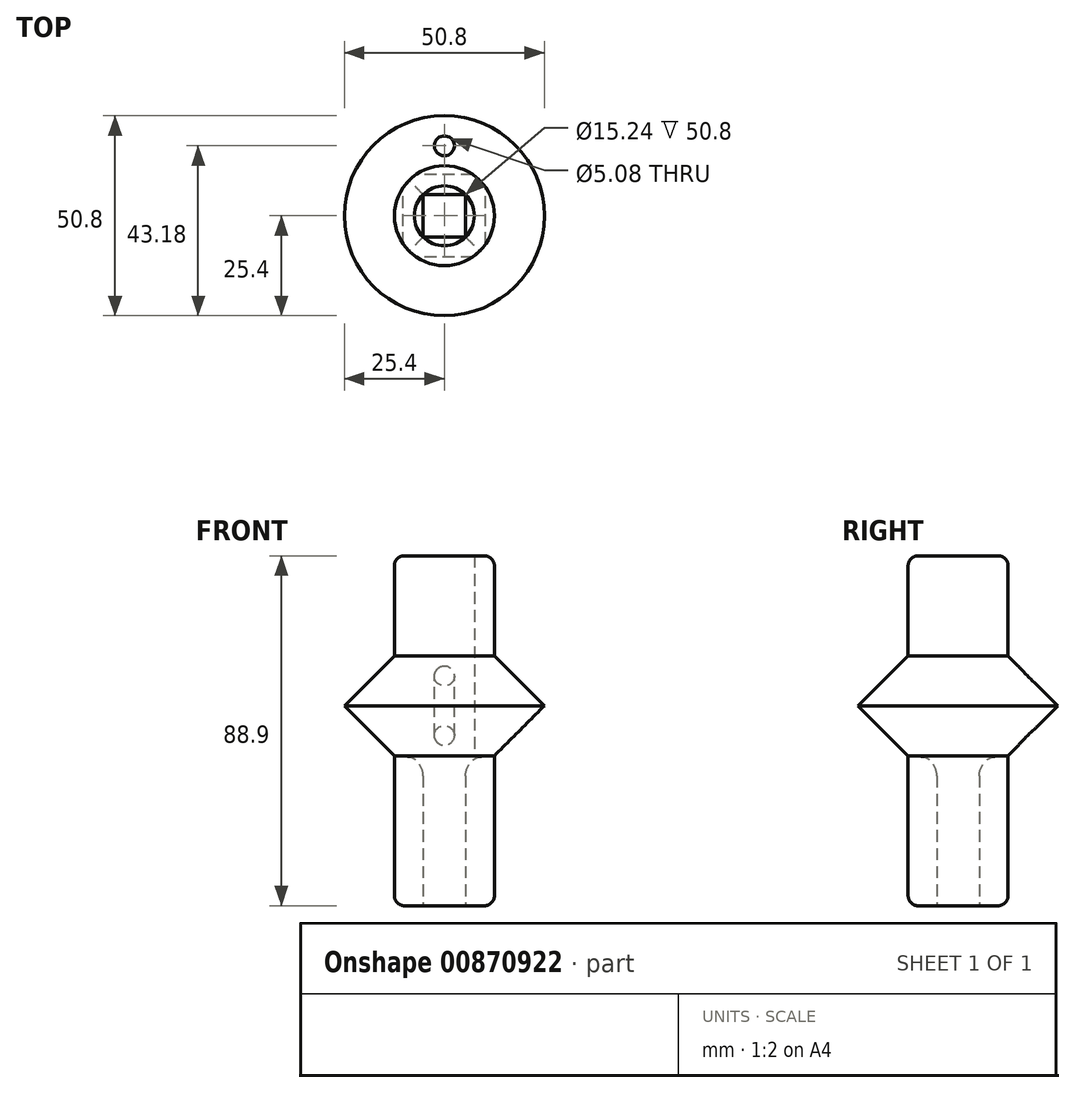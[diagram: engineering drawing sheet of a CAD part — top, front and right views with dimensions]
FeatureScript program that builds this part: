
annotation { "Feature Type Name" : "Feature", "Feature Type Description" : "" }
export const myFeature = defineFeature(function(context is Context, id is Id, definition is map)
    precondition{}
    {
        {
            var Q0;
            Q0=qCreatedBy(makeId("Top.planeOp"),FACE);
            var sketch = newSketch(context, id + "F0", { "sketchPlane" : qUnion([Q0])});
            skCircle(sketch, "E0", {"center": v(0, 0) * mm, "radius": 12.7 * mm});
            skCircle(sketch, "E1", {"center": v(0, 0) * mm, "radius": 7.62 * mm});
            skLineSegment(sketch, "E2.bottom", {"start": v(5.39, -5.39) * mm, "end": v(-5.39, -5.39) * mm});
            skLineSegment(sketch, "E2.top", {"start": v(5.39, 5.39) * mm, "end": v(-5.39, 5.39) * mm});
            skLineSegment(sketch, "E2.left", {"start": v(5.39, -5.39) * mm, "end": v(5.39, 5.39) * mm});
            skLineSegment(sketch, "E2.right", {"start": v(-5.39, -5.39) * mm, "end": v(-5.39, 5.39) * mm});
            skSolve(sketch);
        }
        {
            var Q0;
            Q0=makeQuery(id+"F0.imprint","IMPRINT",FACE,{"disambiguationData":[TD([[makeQuery(id+"F0.imprint","IMPRINT",EDGE,{"derivedFrom":sQuery(id+"F0.wireOp",EDGE,"E0")}),1.0]])]});
            var Q1;
            {var subQ0=sQuery(id+"F0.wireOp",EDGE,"E2.bottom");Q1=makeQuery(id+"F0.imprint","IMPRINT",FACE,{"disambiguationData":[TD([[makeQuery(id+"F0.imprint","IMPRINT",EDGE,{"derivedFrom":subQ0}),1.0]])]});}
            var Q2;
            {var subQ0=sQuery(id+"F0.wireOp",EDGE,"E2.right");Q2=makeQuery(id+"F0.imprint","IMPRINT",FACE,{"disambiguationData":[TD([[makeQuery(id+"F0.imprint","IMPRINT",EDGE,{"derivedFrom":subQ0}),1.0]])]});}
            var Q3;
            {var subQ0=sQuery(id+"F0.wireOp",EDGE,"E2.left");Q3=makeQuery(id+"F0.imprint","IMPRINT",FACE,{"disambiguationData":[TD([[makeQuery(id+"F0.imprint","IMPRINT",EDGE,{"derivedFrom":subQ0}),-1.0]])]});}
            var Q4;
            {var subQ0=sQuery(id+"F0.wireOp",EDGE,"E2.top");Q4=makeQuery(id+"F0.imprint","IMPRINT",FACE,{"disambiguationData":[TD([[makeQuery(id+"F0.imprint","IMPRINT",EDGE,{"derivedFrom":subQ0}),-1.0]])]});}
            extrude(context, id + "F1", {"entities" : qUnion([Q0, Q1, Q2, Q3, Q4]), "depth" : 38.1 * mm, "offsetDistance" : 25.4 * mm});
        }
        {
            var Q0;
            Q0=makeQuery(id+"F1.opExtrude","CAP_FACE",FACE,{"disambiguationData":[OSD([sQuery(id+"F0.wireOp",EDGE,"E0"),sQuery(id+"F0.wireOp",EDGE,"E1")])],"isStart":false});
            var sketch = newSketch(context, id + "F2", { "sketchPlane" : qUnion([Q0])});
            skCircle(sketch, "E3", {"center": v(0, 0) * mm, "radius": 25.4 * mm});
            skSolve(sketch);
        }
        {
            var Q0;
            Q0=makeQuery(id+"F2.imprint","IMPRINT",FACE,{"disambiguationData":[TD([[makeQuery(id+"F2.imprint","IMPRINT",EDGE,{"derivedFrom":sQuery(id+"F2.wireOp",EDGE,"E3")}),1.0]])]});
            extrude(context, id + "F3", {"entities" : qUnion([Q0]), "depth" : 12.7 * mm, "offsetDistance" : 25.4 * mm});
        }
        {
            var Q0;
            Q0=makeQuery(id+"F1.opExtrude","CAP_EDGE",EDGE,{"disambiguationData":[OSD([sQuery(id+"F0.wireOp",EDGE,"E0")])],"isStart":true});
            fillet(context, id + "F4", {"entities" : qUnion([Q0]), "radius" : 2.54 * mm, "tangentPropagation" : true, "allowEdgeOverflow" : false});
        }
        {
            var Q0;
            Q0=makeQuery(id+"F1.opExtrude","CAP_EDGE",EDGE,{"disambiguationData":[OSD([sQuery(id+"F0.wireOp",EDGE,"E2.left")])],"isStart":false});
            var Q1;
            Q1=makeQuery(id+"F1.opExtrude","CAP_EDGE",EDGE,{"disambiguationData":[OSD([sQuery(id+"F0.wireOp",EDGE,"E2.bottom")])],"isStart":false});
            var Q2;
            Q2=makeQuery(id+"F1.opExtrude","CAP_EDGE",EDGE,{"disambiguationData":[OSD([sQuery(id+"F0.wireOp",EDGE,"E2.right")])],"isStart":false});
            var Q3;
            Q3=makeQuery(id+"F1.opExtrude","CAP_EDGE",EDGE,{"disambiguationData":[OSD([sQuery(id+"F0.wireOp",EDGE,"E2.top")])],"isStart":false});
            fillet(context, id + "F5", {"entities" : qUnion([Q0, Q1, Q2, Q3]), "radius" : 5.08 * mm, "tangentPropagation" : true, "allowEdgeOverflow" : false});
        }
        {
            var Q0;
            Q0=makeQuery(id+"F3.opExtrude","SWEPT_BODY",BODY,{"disambiguationData":[OSD([sQuery(id+"F0.wireOp",EDGE,"E0"),sQuery(id+"F2.wireOp",EDGE,"E3")])]});
            var Q1;
            Q1=makeQuery(id+"F3.opExtrude","CAP_FACE",FACE,{"disambiguationData":[OSD([sQuery(id+"F0.wireOp",EDGE,"E0"),sQuery(id+"F2.wireOp",EDGE,"E3")])],"isStart":false});
            mirror(context, id + "F6", {"operationType" : NewBodyOperationType.ADD, "entities" : qUnion([Q0]), "mirrorPlane" : qUnion([Q1])});
        }
        {
            var Q0;
            Q0=makeQuery(id+"F5.opFillet","SPLIT",FACE,{"disambiguationData":[OD(1.0)],"derivedFrom":makeQuery(id+"F1.opExtrude","CAP_FACE",FACE,{"disambiguationData":[OSD([sQuery(id+"F0.wireOp",EDGE,"E0"),sQuery(id+"F0.wireOp",EDGE,"E2.bottom"),sQuery(id+"F0.wireOp",EDGE,"E2.top"),sQuery(id+"F0.wireOp",EDGE,"E2.left"),sQuery(id+"F0.wireOp",EDGE,"E2.right")])],"isStart":false})});
            cPlane(context, id + "F7", {"entities" : qUnion([Q0]), "cplaneType" : CPlaneType.OFFSET, "offset" : 25.4 * mm, "width" : 152.4 * mm, "height" : 152.4 * mm});
        }
        {
            var Q0;
            Q0=qCreatedBy(id+"F7.planeOp",FACE);
            var sketch = newSketch(context, id + "F8", { "sketchPlane" : qUnion([Q0])});
            skCircle(sketch, "E4", {"center": v(0, 0) * mm, "radius": 12.7 * mm});
            skCircle(sketch, "E5", {"center": v(0, 0) * mm, "radius": 7.62 * mm});
            skSolve(sketch);
        }
        {
            var Q0;
            Q0=makeQuery(id+"F8.imprint","IMPRINT",FACE,{"disambiguationData":[TD([[makeQuery(id+"F8.imprint","IMPRINT",EDGE,{"derivedFrom":sQuery(id+"F8.wireOp",EDGE,"E4")}),1.0]])]});
            extrude(context, id + "F9", {"entities" : qUnion([Q0]), "depth" : 25.4 * mm, "offsetDistance" : 25.4 * mm});
        }
        {
            var Q0;
            Q0=makeQuery(id+"F9.opExtrude","CAP_EDGE",EDGE,{"disambiguationData":[OSD([sQuery(id+"F8.wireOp",EDGE,"E4")])],"isStart":false});
            fillet(context, id + "F10", {"entities" : qUnion([Q0]), "radius" : 2.54 * mm, "tangentPropagation" : true, "allowEdgeOverflow" : false});
        }
        {
            var Q0;
            Q0=qSketchRegion(id+"F8",true);
            extrude(context, id + "F11", {"entities" : qUnion([Q0]), "operationType" : NewBodyOperationType.ADD, "oppositeDirection" : true, "depth" : 25.4 * mm, "offsetDistance" : 25.4 * mm});
        }
        {
            var Q0;
            Q0=makeQuery(id+"F3.opExtrude","CAP_EDGE",EDGE,{"disambiguationData":[OSD([sQuery(id+"F2.wireOp",EDGE,"E3")])],"isStart":true});
            var Q1;
            Q1=makeQuery(id+"F6.opPattern","COPY",EDGE,{"derivedFrom":makeQuery(id+"F3.opExtrude","CAP_EDGE",EDGE,{"disambiguationData":[OSD([sQuery(id+"F2.wireOp",EDGE,"E3")])],"isStart":true}),"instanceName":"1"});
            chamfer(context, id + "F12", {"entities" : qUnion([Q0, Q1]), "width" : 12.7 * mm, "tangentPropagation" : true});
        }
        {
            var Q0;
            Q0=makeQuery(id+"F9.opExtrude","CAP_FACE",FACE,{"disambiguationData":[OSD([sQuery(id+"F8.wireOp",EDGE,"E4"),sQuery(id+"F8.wireOp",EDGE,"E5")])],"isStart":false});
            var sketch = newSketch(context, id + "F13", { "sketchPlane" : qUnion([Q0])});
            skLineSegment(sketch, "E6", {"start": v(0, 0) * mm, "end": v(0, 17.78) * mm, "construction": true});
            skCircle(sketch, "E7", {"center": v(0, 17.78) * mm, "radius": 2.54 * mm});
            skSolve(sketch);
        }
        {
            var Q0;
            Q0=makeQuery(id+"F13.imprint","IMPRINT",FACE,{"disambiguationData":[TD([[makeQuery(id+"F13.imprint","IMPRINT",EDGE,{"derivedFrom":sQuery(id+"F13.wireOp",EDGE,"E7")}),1.0]])]});
            extrude(context, id + "F14", {"entities" : qUnion([Q0]), "operationType" : NewBodyOperationType.REMOVE, "oppositeDirection" : true, "depth" : 152.4 * mm, "offsetDistance" : 25.4 * mm});
        }
    });
